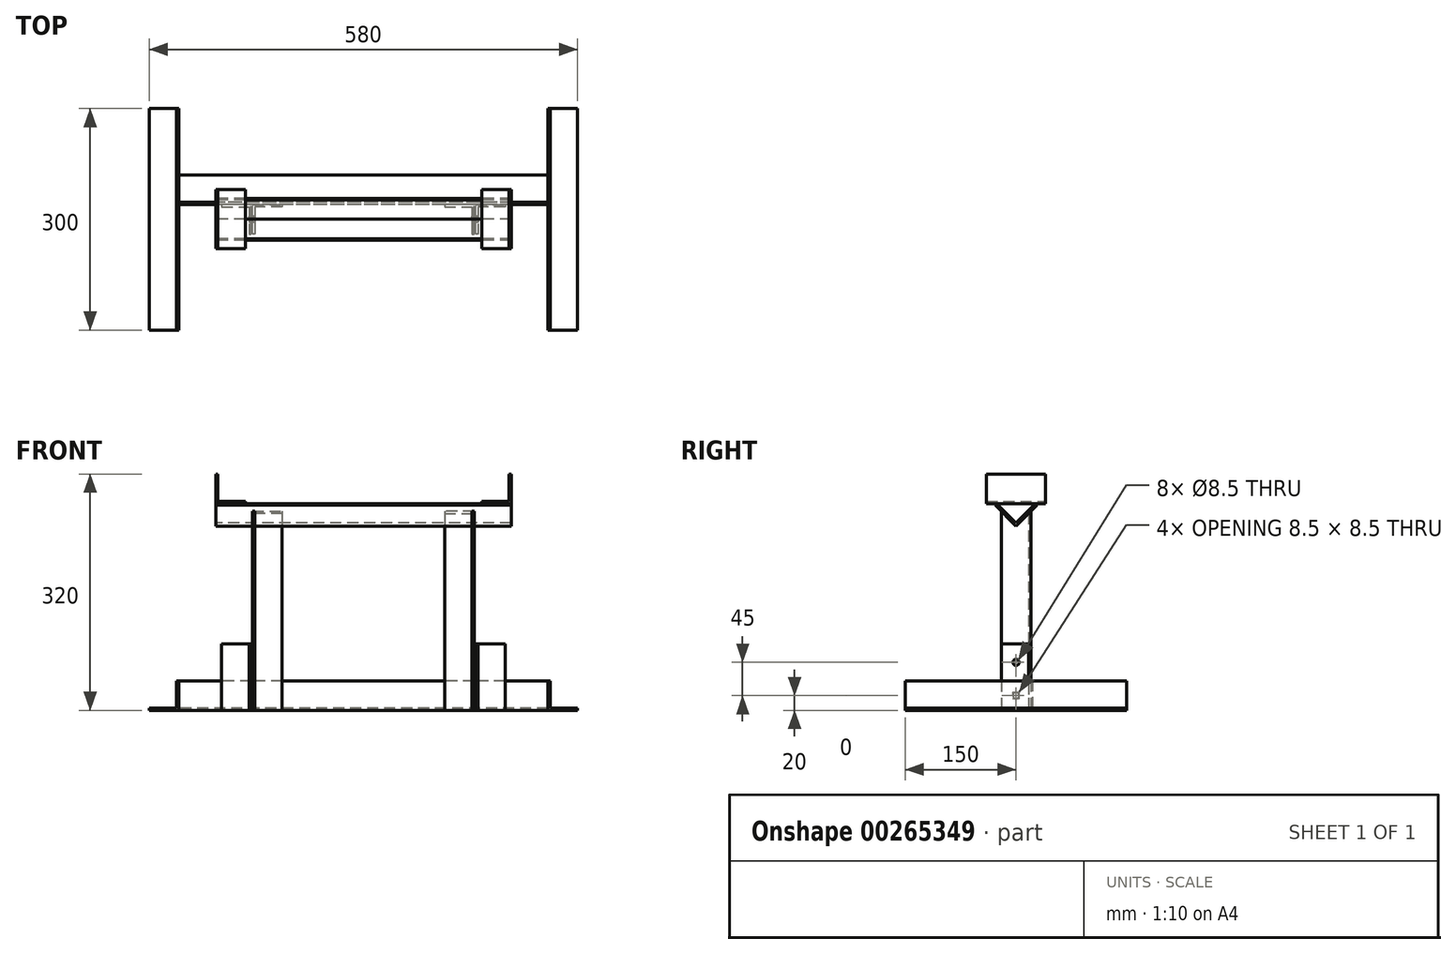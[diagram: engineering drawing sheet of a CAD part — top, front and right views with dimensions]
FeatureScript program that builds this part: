
annotation { "Feature Type Name" : "Feature", "Feature Type Description" : "" }
export const myFeature = defineFeature(function(context is Context, id is Id, definition is map)
    precondition{}
    {
        {
            var Q0;
            Q0=qCreatedBy(makeId("Right.planeOp"),FACE);
            var sketch = newSketch(context, id + "F0", { "sketchPlane" : qUnion([Q0])});
            skLineSegment(sketch, "E0", {"start": v(-28.28, 277.88) * mm, "end": v(0, 249.6) * mm});
            skLineSegment(sketch, "E1", {"start": v(0, 249.6) * mm, "end": v(28.28, 277.88) * mm});
            skLineSegment(sketch, "E2", {"start": v(-26.16, 280) * mm, "end": v(-28.28, 277.88) * mm});
            skLineSegment(sketch, "E3", {"start": v(-26.16, 280) * mm, "end": v(0, 253.84) * mm});
            skLineSegment(sketch, "E4", {"start": v(0, 253.84) * mm, "end": v(26.16, 280) * mm});
            skLineSegment(sketch, "E5", {"start": v(26.16, 280) * mm, "end": v(28.28, 277.88) * mm});
            skLineSegment(sketch, "E6", {"start": v(0, 0) * mm, "end": v(0, 249.6) * mm, "construction": true});
            skSolve(sketch);
        }
        {
            var Q0;
            Q0=makeQuery(id+"F0.imprint","IMPRINT",FACE,{"disambiguationData":[TD([[makeQuery(id+"F0.imprint","IMPRINT",EDGE,{"derivedFrom":sQuery(id+"F0.wireOp",EDGE,"E0")}),1.0]])]});
            extrude(context, id + "F1", {"entities" : qUnion([Q0]), "depth" : 200 * mm, "hasSecondDirection" : true, "secondDirectionOppositeDirection" : true, "secondDirectionDepth" : 200 * mm});
        }
        {
            var Q0;
            Q0=qCreatedBy(makeId("Front.planeOp"),FACE);
            var sketch = newSketch(context, id + "F2", { "sketchPlane" : qUnion([Q0])});
            skLineSegment(sketch, "E7.0", {"start": v(200, 280) * mm, "end": v(-200, 280) * mm});
            skLineSegment(sketch, "E8", {"start": v(200, 280) * mm, "end": v(200, 320) * mm});
            skLineSegment(sketch, "E9", {"start": v(200, 320) * mm, "end": v(197, 320) * mm});
            skLineSegment(sketch, "E10", {"start": v(197, 320) * mm, "end": v(197, 283) * mm});
            skLineSegment(sketch, "E11", {"start": v(197, 283) * mm, "end": v(160, 283) * mm});
            skLineSegment(sketch, "E12", {"start": v(160, 283) * mm, "end": v(160, 280) * mm});
            skLineSegment(sketch, "E13", {"start": v(0, 0) * mm, "end": v(0, 317.14) * mm, "construction": true});
            skLineSegment(sketch, "E14.MirrorCS", {"start": v(-200, 320) * mm, "end": v(-197, 320) * mm});
            skLineSegment(sketch, "E15.MirrorCS", {"start": v(-160, 283) * mm, "end": v(-160, 280) * mm});
            skLineSegment(sketch, "E16.MirrorCS", {"start": v(-197, 283) * mm, "end": v(-160, 283) * mm});
            skLineSegment(sketch, "E17.MirrorCS", {"start": v(-200, 280) * mm, "end": v(200, 280) * mm});
            skLineSegment(sketch, "E18.MirrorCS", {"start": v(-200, 280) * mm, "end": v(-200, 320) * mm});
            skLineSegment(sketch, "E19.MirrorCS", {"start": v(-197, 320) * mm, "end": v(-197, 283) * mm});
            skSolve(sketch);
        }
        {
            var Q0;
            Q0=makeQuery(id+"F2.imprint","IMPRINT",FACE,{"disambiguationData":[TD([[makeQuery(id+"F2.imprint","IMPRINT",EDGE,{"derivedFrom":sQuery(id+"F2.wireOp",EDGE,"E14.MirrorCS")}),-1.0]])]});
            var Q1;
            {var subQ1=sQuery(id+"F2.wireOp",EDGE,"E8");Q1=makeQuery(id+"F2.imprint","IMPRINT",FACE,{"disambiguationData":[TD([[makeQuery(id+"F2.imprint","IMPRINT",EDGE,{"derivedFrom":subQ1}),1.0]])]});}
            extrude(context, id + "F3", {"entities" : qUnion([Q0, Q1]), "depth" : 40 * mm, "hasSecondDirection" : true, "secondDirectionOppositeDirection" : true, "secondDirectionDepth" : 40 * mm});
        }
        {
            var Q0;
            Q0=qCreatedBy(makeId("Top.planeOp"),FACE);
            var sketch = newSketch(context, id + "F4", { "sketchPlane" : qUnion([Q0])});
            skLineSegment(sketch, "E20", {"start": v(-150, -20) * mm, "end": v(-150, 20) * mm});
            skLineSegment(sketch, "E21", {"start": v(-150, 20) * mm, "end": v(-110, 20) * mm});
            skLineSegment(sketch, "E22", {"start": v(-110, 20) * mm, "end": v(-110, 17) * mm});
            skLineSegment(sketch, "E23", {"start": v(-110, 17) * mm, "end": v(-147, 17) * mm});
            skLineSegment(sketch, "E24", {"start": v(-147, 17) * mm, "end": v(-147, -20) * mm});
            skLineSegment(sketch, "E25", {"start": v(-147, -20) * mm, "end": v(-150, -20) * mm});
            skLineSegment(sketch, "E26", {"start": v(0, 0) * mm, "end": v(0, 123.27) * mm, "construction": true});
            skLineSegment(sketch, "E27.MirrorCS", {"start": v(110, 20) * mm, "end": v(110, 17) * mm});
            skLineSegment(sketch, "E28.MirrorCS", {"start": v(147, -20) * mm, "end": v(150, -20) * mm});
            skLineSegment(sketch, "E29.MirrorCS", {"start": v(150, -20) * mm, "end": v(150, 20) * mm});
            skLineSegment(sketch, "E30.MirrorCS", {"start": v(150, 20) * mm, "end": v(110, 20) * mm});
            skLineSegment(sketch, "E31.MirrorCS", {"start": v(147, 17) * mm, "end": v(147, -20) * mm});
            skLineSegment(sketch, "E32.MirrorCS", {"start": v(110, 17) * mm, "end": v(147, 17) * mm});
            skSolve(sketch);
        }
        {
            var Q0;
            Q0=makeQuery(id+"F4.imprint","IMPRINT",FACE,{"disambiguationData":[TD([[makeQuery(id+"F4.imprint","IMPRINT",EDGE,{"derivedFrom":sQuery(id+"F4.wireOp",EDGE,"E20")}),-1.0]])]});
            var Q1;
            Q1=makeQuery(id+"F4.imprint","IMPRINT",FACE,{"disambiguationData":[TD([[makeQuery(id+"F4.imprint","IMPRINT",EDGE,{"derivedFrom":sQuery(id+"F4.wireOp",EDGE,"E27.MirrorCS")}),1.0]])]});
            var Q2;
            Q2=makeQuery(id+"F1.opExtrude","SWEPT_BODY",BODY,{"disambiguationData":[OSD([sQuery(id+"F0.wireOp",EDGE,"E0"),sQuery(id+"F0.wireOp",EDGE,"E1"),sQuery(id+"F0.wireOp",EDGE,"E2"),sQuery(id+"F0.wireOp",EDGE,"E3"),sQuery(id+"F0.wireOp",EDGE,"E4"),sQuery(id+"F0.wireOp",EDGE,"E5")])]});
            extrude(context, id + "F5", {"entities" : qUnion([Q0, Q1]), "endBound" : BoundingType.UP_TO_BODY, "endBoundEntityBody" : qUnion([Q2]), "depth" : 25 * mm});
        }
        {
            var Q0;
            Q0=qCreatedBy(makeId("Right.planeOp"),FACE);
            var sketch = newSketch(context, id + "F6", { "sketchPlane" : qUnion([Q0])});
            skLineSegment(sketch, "E33", {"start": v(20, 0) * mm, "end": v(60, 0) * mm});
            skLineSegment(sketch, "E34", {"start": v(60, 0) * mm, "end": v(60, 3) * mm});
            skLineSegment(sketch, "E35", {"start": v(60, 3) * mm, "end": v(23, 3) * mm});
            skLineSegment(sketch, "E36", {"start": v(23, 3) * mm, "end": v(23, 40) * mm});
            skLineSegment(sketch, "E37", {"start": v(23, 40) * mm, "end": v(20, 40) * mm});
            skLineSegment(sketch, "E38", {"start": v(20, 40) * mm, "end": v(20, 0) * mm});
            skSolve(sketch);
        }
        {
            var Q0;
            Q0=makeQuery(id+"F6.imprint","IMPRINT",FACE,{"disambiguationData":[TD([[makeQuery(id+"F6.imprint","IMPRINT",EDGE,{"derivedFrom":sQuery(id+"F6.wireOp",EDGE,"E33")}),1.0]])]});
            extrude(context, id + "F7", {"entities" : qUnion([Q0]), "depth" : 250 * mm, "hasSecondDirection" : true, "secondDirectionOppositeDirection" : true, "secondDirectionDepth" : 250 * mm});
        }
        {
            var Q0;
            Q0=qCreatedBy(makeId("Front.planeOp"),FACE);
            var sketch = newSketch(context, id + "F8", { "sketchPlane" : qUnion([Q0])});
            skLineSegment(sketch, "E39", {"start": v(-250, 0) * mm, "end": v(-250, 40) * mm});
            skLineSegment(sketch, "E40", {"start": v(-250, 40) * mm, "end": v(-253, 40) * mm});
            skLineSegment(sketch, "E41", {"start": v(-253, 40) * mm, "end": v(-253, 3) * mm});
            skLineSegment(sketch, "E42", {"start": v(-253, 3) * mm, "end": v(-290, 3) * mm});
            skLineSegment(sketch, "E43", {"start": v(-290, 3) * mm, "end": v(-290, 0) * mm});
            skLineSegment(sketch, "E44", {"start": v(-290, 0) * mm, "end": v(-250, 0) * mm});
            skLineSegment(sketch, "E45", {"start": v(0, 0) * mm, "end": v(0, -68.45) * mm, "construction": true});
            skLineSegment(sketch, "E46.MirrorCS", {"start": v(250, 40) * mm, "end": v(253, 40) * mm});
            skLineSegment(sketch, "E47.MirrorCS", {"start": v(290, 3) * mm, "end": v(290, 0) * mm});
            skLineSegment(sketch, "E48.MirrorCS", {"start": v(250, 0) * mm, "end": v(250, 40) * mm});
            skLineSegment(sketch, "E49.MirrorCS", {"start": v(253, 40) * mm, "end": v(253, 3) * mm});
            skLineSegment(sketch, "E50.MirrorCS", {"start": v(290, 0) * mm, "end": v(250, 0) * mm});
            skLineSegment(sketch, "E51.MirrorCS", {"start": v(253, 3) * mm, "end": v(290, 3) * mm});
            skSolve(sketch);
        }
        {
            var Q0;
            Q0=makeQuery(id+"F8.imprint","IMPRINT",FACE,{"disambiguationData":[TD([[makeQuery(id+"F8.imprint","IMPRINT",EDGE,{"derivedFrom":sQuery(id+"F8.wireOp",EDGE,"E39")}),1.0]])]});
            var Q1;
            Q1=makeQuery(id+"F8.imprint","IMPRINT",FACE,{"disambiguationData":[TD([[makeQuery(id+"F8.imprint","IMPRINT",EDGE,{"derivedFrom":sQuery(id+"F8.wireOp",EDGE,"E46.MirrorCS")}),-1.0]])]});
            extrude(context, id + "F9", {"entities" : qUnion([Q0, Q1]), "depth" : 150 * mm, "hasSecondDirection" : true, "secondDirectionOppositeDirection" : true, "secondDirectionDepth" : 150 * mm});
        }
        {
            var Q0;
            Q0=qCreatedBy(makeId("Top.planeOp"),FACE);
            var sketch = newSketch(context, id + "F10", { "sketchPlane" : qUnion([Q0])});
            skLineSegment(sketch, "E52", {"start": v(-152, -20) * mm, "end": v(-152, 20) * mm});
            skLineSegment(sketch, "E53", {"start": v(-152, 20) * mm, "end": v(-192, 20) * mm});
            skLineSegment(sketch, "E54", {"start": v(-192, 20) * mm, "end": v(-192, 17) * mm});
            skLineSegment(sketch, "E55", {"start": v(-192, 17) * mm, "end": v(-155, 17) * mm});
            skLineSegment(sketch, "E56", {"start": v(-155, 17) * mm, "end": v(-155, -20) * mm});
            skLineSegment(sketch, "E57", {"start": v(-155, -20) * mm, "end": v(-152, -20) * mm});
            skLineSegment(sketch, "E58", {"start": v(0, 0) * mm, "end": v(0, 112.46) * mm, "construction": true});
            skLineSegment(sketch, "E59.MirrorCS", {"start": v(192, 20) * mm, "end": v(192, 17) * mm});
            skLineSegment(sketch, "E60.MirrorCS", {"start": v(155, -20) * mm, "end": v(152, -20) * mm});
            skLineSegment(sketch, "E61.MirrorCS", {"start": v(152, 20) * mm, "end": v(192, 20) * mm});
            skLineSegment(sketch, "E62.MirrorCS", {"start": v(192, 17) * mm, "end": v(155, 17) * mm});
            skLineSegment(sketch, "E63.MirrorCS", {"start": v(155, 17) * mm, "end": v(155, -20) * mm});
            skLineSegment(sketch, "E64.MirrorCS", {"start": v(152, -20) * mm, "end": v(152, 20) * mm});
            skSolve(sketch);
        }
        {
            var Q0;
            Q0=makeQuery(id+"F10.imprint","IMPRINT",FACE,{"disambiguationData":[TD([[makeQuery(id+"F10.imprint","IMPRINT",EDGE,{"derivedFrom":sQuery(id+"F10.wireOp",EDGE,"E52")}),1.0]])]});
            var Q1;
            Q1=makeQuery(id+"F10.imprint","IMPRINT",FACE,{"disambiguationData":[TD([[makeQuery(id+"F10.imprint","IMPRINT",EDGE,{"derivedFrom":sQuery(id+"F10.wireOp",EDGE,"E59.MirrorCS")}),-1.0]])]});
            extrude(context, id + "F11", {"entities" : qUnion([Q0, Q1]), "depth" : 90 * mm});
        }
        {
            var Q0;
            Q0=qCreatedBy(makeId("Right.planeOp"),FACE);
            var sketch = newSketch(context, id + "F12", { "sketchPlane" : qUnion([Q0])});
            skCircle(sketch, "E65", {"center": v(0, 20) * mm, "radius": 4.25 * mm});
            skCircle(sketch, "E66", {"center": v(0, 65) * mm, "radius": 4.25 * mm});
            skSolve(sketch);
        }
        {
            var Q0;
            Q0=makeQuery(id+"F12.imprint","IMPRINT",FACE,{"disambiguationData":[TD([[makeQuery(id+"F12.imprint","IMPRINT",EDGE,{"derivedFrom":sQuery(id+"F12.wireOp",EDGE,"E66")}),1.0]])]});
            var Q1;
            Q1=makeQuery(id+"F12.imprint","IMPRINT",FACE,{"disambiguationData":[TD([[makeQuery(id+"F12.imprint","IMPRINT",EDGE,{"derivedFrom":sQuery(id+"F12.wireOp",EDGE,"E65")}),1.0]])]});
            var Q2;
            Q2=makeQuery(id+"F11.opExtrude","SWEPT_FACE",FACE,{"disambiguationData":[OSD([sQuery(id+"F10.wireOp",EDGE,"E63.MirrorCS")])]});
            var Q3;
            Q3=makeQuery(id+"F11.opExtrude","SWEPT_FACE",FACE,{"disambiguationData":[OSD([sQuery(id+"F10.wireOp",EDGE,"E56")])]});
            extrude(context, id + "F13", {"entities" : qUnion([Q0, Q1]), "operationType" : NewBodyOperationType.REMOVE, "endBound" : BoundingType.UP_TO_SURFACE, "endBoundEntityFace" : qUnion([Q2]), "depth" : 25 * mm, "hasSecondDirection" : true, "secondDirectionBound" : SecondDirectionBoundingType.UP_TO_SURFACE, "secondDirectionOppositeDirection" : true, "secondDirectionBoundEntityFace" : qUnion([Q3]), "secondDirectionDepth" : 25 * mm});
        }
    });
